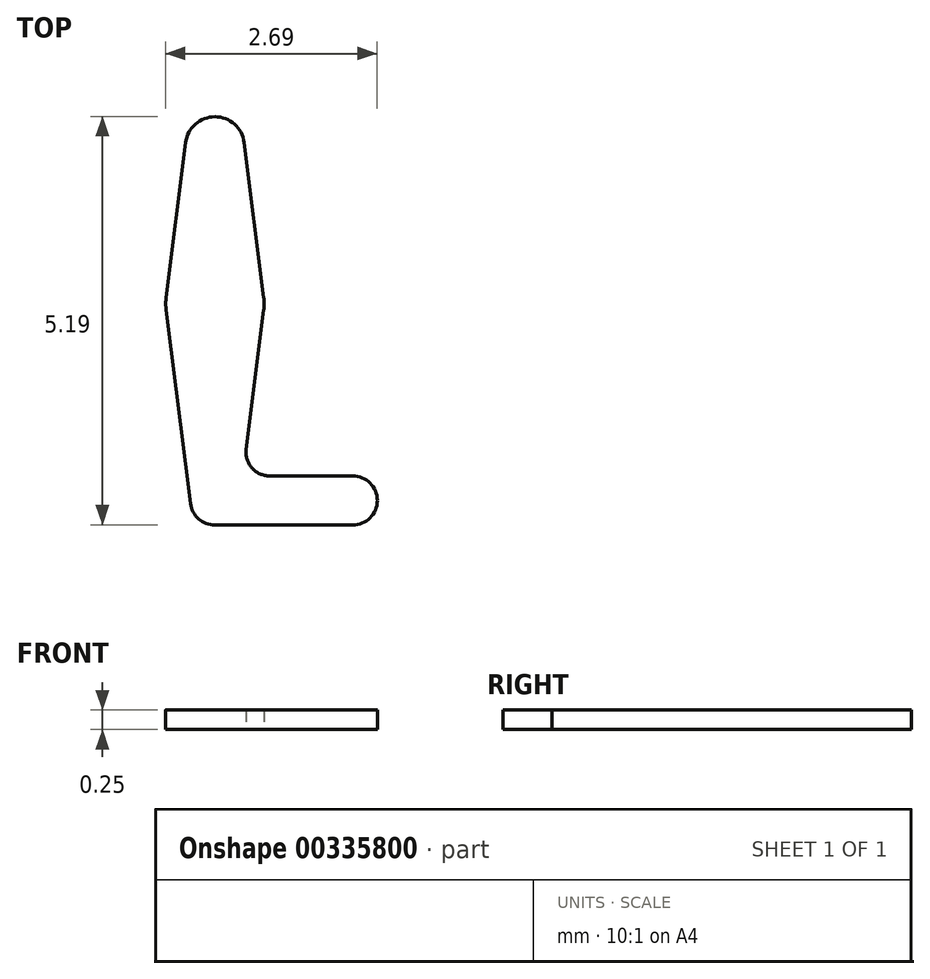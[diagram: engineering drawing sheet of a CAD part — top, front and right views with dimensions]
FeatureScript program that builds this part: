
annotation { "Feature Type Name" : "Feature", "Feature Type Description" : "" }
export const myFeature = defineFeature(function(context is Context, id is Id, definition is map)
    precondition{}
    {
        {
            var Q0;
            Q0=qCreatedBy(makeId("Top.planeOp"),FACE);
            var sketch = newSketch(context, id + "F0", { "sketchPlane" : qUnion([Q0])});
            skLineSegment(sketch, "E0", {"start": v(0, 4.5) * mm, "end": v(0, 0) * mm, "construction": true});
            skLineSegment(sketch, "E1", {"start": v(0, 0) * mm, "end": v(1.75, 0) * mm, "construction": true});
            skCircle(sketch, "E2", {"center": v(0, 4.5) * mm, "radius": 0.38 * mm});
            skCircle(sketch, "E3", {"center": v(0, 2.5) * mm, "radius": 0.62 * mm});
            skCircle(sketch, "E4", {"center": v(1.75, 0) * mm, "radius": 0.31 * mm});
            skLineSegment(sketch, "E5", {"start": v(-0.62, 2.58) * mm, "end": v(-0.37, 4.55) * mm});
            skLineSegment(sketch, "E6", {"start": v(-0.37, 4.55) * mm, "end": v(0.37, 4.55) * mm});
            skLineSegment(sketch, "E7", {"start": v(0.37, 4.55) * mm, "end": v(0.62, 2.58) * mm});
            skCircle(sketch, "E8", {"center": v(0, 0) * mm, "radius": 0.31 * mm});
            skLineSegment(sketch, "E9", {"start": v(-0.62, 2.42) * mm, "end": v(-0.31, -0.04) * mm});
            skLineSegment(sketch, "E10", {"start": v(0.62, 2.42) * mm, "end": v(0.4, 0.65) * mm});
            skLineSegment(sketch, "E11", {"start": v(0.7, 0.31) * mm, "end": v(1.75, 0.31) * mm});
            skLineSegment(sketch, "E12", {"start": v(0, -0.31) * mm, "end": v(1.75, -0.31) * mm});
            skArc(sketch, "E13.filletArc", {"start": v(0.4, 0.65) * mm, "mid": v(0.47, 0.41) * mm, "end": v(0.7, 0.31) * mm});
            skSolve(sketch);
        }
        {
            var Q0;
            {var subQ0=sQuery(id+"F0.wireOp",EDGE,"E6");Q0=makeQuery(id+"F0.imprint","IMPRINT",FACE,{"disambiguationData":[TD([[makeQuery(id+"F0.imprint","IMPRINT",EDGE,{"derivedFrom":subQ0}),1.0]])]});}
            var Q1;
            {var subQ0=sQuery(id+"F0.wireOp",EDGE,"E6");Q1=makeQuery(id+"F0.imprint","IMPRINT",FACE,{"disambiguationData":[TD([[makeQuery(id+"F0.imprint","IMPRINT",EDGE,{"derivedFrom":subQ0}),-1.0]])]});}
            var Q2;
            {var subQ1=sQuery(id+"F0.wireOp",EDGE,"E5");Q2=makeQuery(id+"F0.imprint","IMPRINT",FACE,{"disambiguationData":[TD([[makeQuery(id+"F0.imprint","IMPRINT",EDGE,{"derivedFrom":subQ1}),-1.0]])]});}
            var Q3;
            {var subQ0=sQuery(id+"F0.wireOp",EDGE,"E3");var subQ1=makeQuery(id+"F0.imprint","INTERSECT",VERTEX,{"derivedFrom":[subQ0,sQuery(id+"F0.wireOp",EDGE,"E5")]});Q3=makeQuery(id+"F0.imprint","IMPRINT",FACE,{"disambiguationData":[TD([[makeQuery(id+"F0.imprint","IMPRINT",EDGE,{"disambiguationData":[TD([[subQ1,1.0]])],"derivedFrom":subQ0}),1.0]])]});}
            var Q4;
            {var subQ0=sQuery(id+"F0.wireOp",EDGE,"E8");var subQ1=makeQuery(id+"F0.imprint","INTERSECT",VERTEX,{"derivedFrom":[subQ0,sQuery(id+"F0.wireOp",EDGE,"E9")]});Q4=makeQuery(id+"F0.imprint","IMPRINT",FACE,{"disambiguationData":[TD([[makeQuery(id+"F0.imprint","IMPRINT",EDGE,{"disambiguationData":[TD([[subQ1,-1.0]])],"derivedFrom":subQ0}),1.0]])]});}
            var Q5;
            {var subQ0=sQuery(id+"F0.wireOp",EDGE,"E4");var subQ1=makeQuery(id+"F0.imprint","INTERSECT",VERTEX,{"derivedFrom":[subQ0,sQuery(id+"F0.wireOp",EDGE,"E11")]});Q5=makeQuery(id+"F0.imprint","IMPRINT",FACE,{"disambiguationData":[TD([[makeQuery(id+"F0.imprint","IMPRINT",EDGE,{"disambiguationData":[TD([[subQ1,-1.0]])],"derivedFrom":subQ0}),1.0]])]});}
            var Q6;
            {var subQ0=sQuery(id+"F0.wireOp",EDGE,"E9");Q6=makeQuery(id+"F0.imprint","IMPRINT",FACE,{"disambiguationData":[TD([[makeQuery(id+"F0.imprint","IMPRINT",EDGE,{"derivedFrom":subQ0}),1.0]])]});}
            extrude(context, id + "F1", {"entities" : qUnion([Q0, Q1, Q2, Q3, Q4, Q5, Q6]), "depth" : 0.25 * mm});
        }
    });
